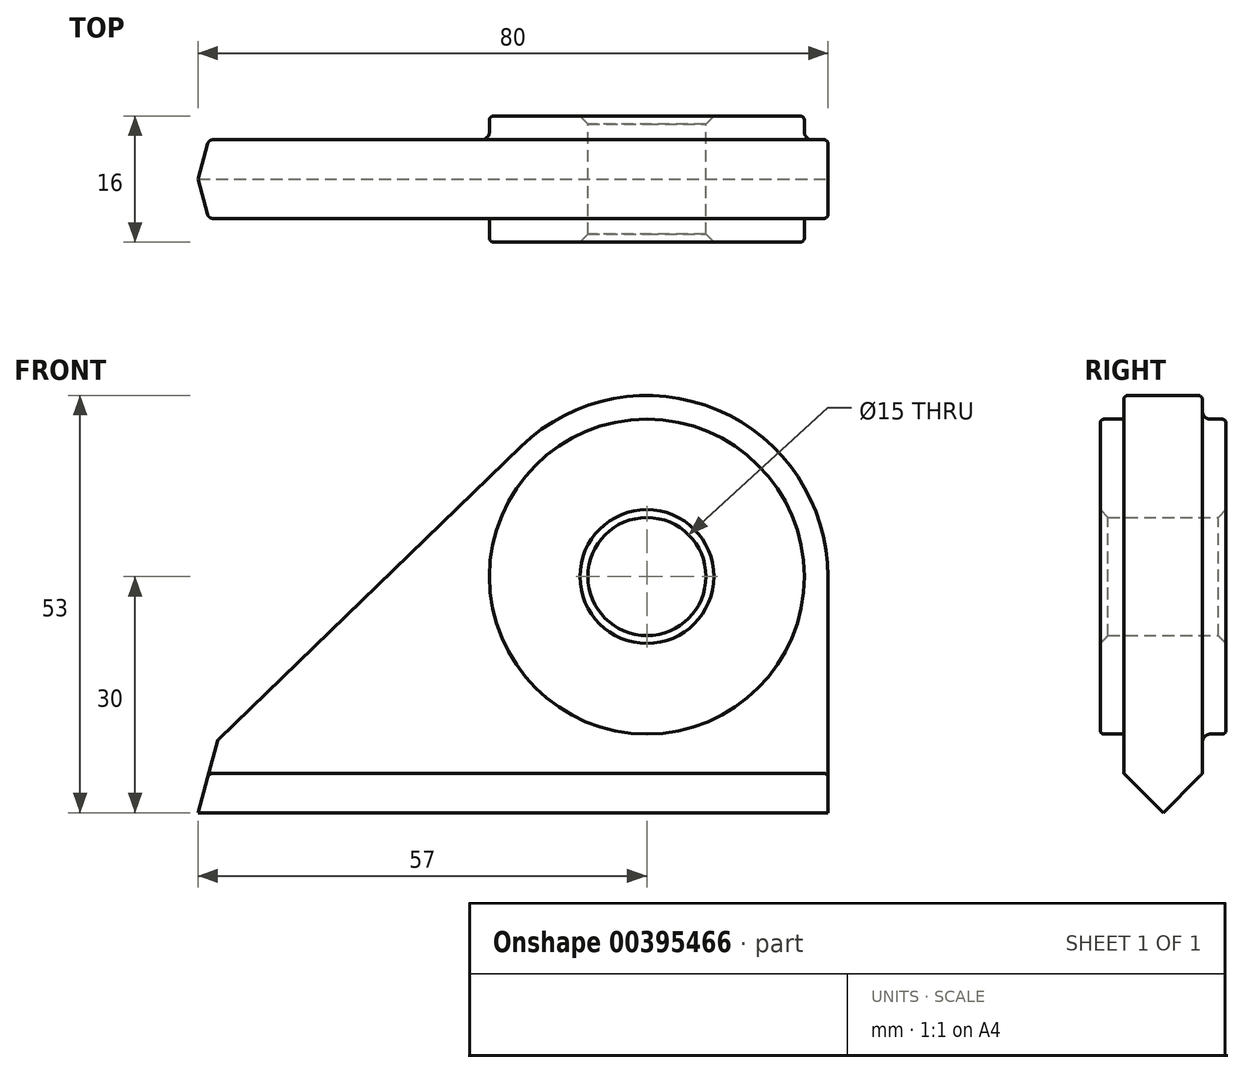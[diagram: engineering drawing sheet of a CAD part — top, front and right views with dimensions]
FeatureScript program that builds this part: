
annotation { "Feature Type Name" : "Feature", "Feature Type Description" : "" }
export const myFeature = defineFeature(function(context is Context, id is Id, definition is map)
    precondition{}
    {
        {
            var Q0;
            Q0=qCreatedBy(makeId("Front.planeOp"),FACE);
            var sketch = newSketch(context, id + "F0", { "sketchPlane" : qUnion([Q0])});
            skCircle(sketch, "E0", {"center": v(0, 0) * mm, "radius": 7.5 * mm});
            skCircle(sketch, "E1", {"center": v(0, 0) * mm, "radius": 20 * mm});
            skArc(sketch, "E2.0", {"start": v(23, 0) * mm, "mid": v(8.98, 21.18) * mm, "end": v(-16, 16.53) * mm});
            skLineSegment(sketch, "E3", {"start": v(23, 0) * mm, "end": v(23, -30) * mm});
            skLineSegment(sketch, "E4", {"start": v(23, -30) * mm, "end": v(-57, -30) * mm});
            skLineSegment(sketch, "E5", {"start": v(-57, -30) * mm, "end": v(-54.52, -20.75) * mm});
            skLineSegment(sketch, "E6", {"start": v(-54.52, -20.75) * mm, "end": v(-16, 16.53) * mm});
            skSolve(sketch);
        }
        {
            var Q0;
            Q0=makeQuery(id+"F0.imprint","IMPRINT",FACE,{"disambiguationData":[TD([[makeQuery(id+"F0.imprint","IMPRINT",EDGE,{"derivedFrom":sQuery(id+"F0.wireOp",EDGE,"E1")}),-1.0]])]});
            extrude(context, id + "F1", {"entities" : qUnion([Q0]), "endBound" : BoundingType.SYMMETRIC, "depth" : 10 * mm});
        }
        {
            var Q0;
            Q0=makeQuery(id+"F0.imprint","IMPRINT",FACE,{"disambiguationData":[TD([[makeQuery(id+"F0.imprint","IMPRINT",EDGE,{"derivedFrom":sQuery(id+"F0.wireOp",EDGE,"E0")}),-1.0]])]});
            extrude(context, id + "F2", {"entities" : qUnion([Q0]), "operationType" : NewBodyOperationType.ADD, "endBound" : BoundingType.SYMMETRIC, "depth" : 16 * mm});
        }
        {
            var Q0;
            Q0=makeQuery(id+"F1.opExtrude","CAP_EDGE",EDGE,{"disambiguationData":[OSD([sQuery(id+"F0.wireOp",EDGE,"E1")])],"isStart":false});
            var Q1;
            Q1=makeQuery(id+"F1.opExtrude","CAP_EDGE",EDGE,{"disambiguationData":[OSD([sQuery(id+"F0.wireOp",EDGE,"E1")])],"isStart":true});
            fillet(context, id + "F3", {"entities" : qUnion([Q0, Q1]), "radius" : 1 * mm, "tangentPropagation" : true, "allowEdgeOverflow" : false});
        }
        {
            var Q0;
            Q0=makeQuery(id+"F2.opExtrude","SWEPT_FACE",FACE,{"disambiguationData":[OSD([sQuery(id+"F0.wireOp",EDGE,"E0")])]});
            chamfer(context, id + "F4", {"entities" : qUnion([Q0]), "width" : 1 * mm, "tangentPropagation" : true});
        }
        {
            var Q0;
            Q0=makeQuery(id+"F1.opExtrude","SWEPT_FACE",FACE,{"disambiguationData":[OSD([sQuery(id+"F0.wireOp",EDGE,"E3")])]});
            var sketch = newSketch(context, id + "F5", { "sketchPlane" : qUnion([Q0])});
            skLineSegment(sketch, "E7", {"start": v(0, 0) * mm, "end": v(0, -30) * mm, "construction": true});
            skLineSegment(sketch, "E8", {"start": v(0, -30) * mm, "end": v(5, -25) * mm});
            skLineSegment(sketch, "E9.MirrorCS", {"start": v(0, -30) * mm, "end": v(-5, -25) * mm});
            skLineSegment(sketch, "E10", {"start": v(5, -25) * mm, "end": v(8.4, -25) * mm});
            skLineSegment(sketch, "E11", {"start": v(8.4, -25) * mm, "end": v(8.4, -34.27) * mm});
            skLineSegment(sketch, "E12", {"start": v(8.4, -34.27) * mm, "end": v(0, -34.27) * mm});
            skLineSegment(sketch, "E13.MirrorCS", {"start": v(-5, -25) * mm, "end": v(-8.4, -25) * mm});
            skLineSegment(sketch, "E14.MirrorCS", {"start": v(-8.4, -25) * mm, "end": v(-8.4, -34.27) * mm});
            skLineSegment(sketch, "E15.MirrorCS", {"start": v(-8.4, -34.27) * mm, "end": v(0, -34.27) * mm});
            skSolve(sketch);
        }
        {
            var Q0;
            Q0 = qSketchRegion(id + "F5", true);
            extrude(context, id + "F6", {"entities" : qUnion([Q0]), "operationType" : NewBodyOperationType.REMOVE, "endBound" : BoundingType.THROUGH_ALL, "oppositeDirection" : true, "depth" : 25 * mm});
        }
        {
            var Q0;
            Q0=makeQuery(id+"F2.opExtrude","CAP_EDGE",EDGE,{"disambiguationData":[OSD([sQuery(id+"F0.wireOp",EDGE,"E1")])],"isStart":false});
            var Q1;
            Q1=makeQuery(id+"F2.opExtrude","CAP_EDGE",EDGE,{"disambiguationData":[OSD([sQuery(id+"F0.wireOp",EDGE,"E1")])],"isStart":true});
            var Q2;
            Q2=makeQuery(id+"F6.boolean.opBoolean","COPY",EDGE,{"derivedFrom":makeQuery(id+"F6.opExtrude","SWEPT_EDGE",EDGE,{"disambiguationData":[OSD([sQuery(id+"F0.wireOp",EDGE,"E3"),sQuery(id+"F5.wireOp",EDGE,"E8"),sQuery(id+"F5.wireOp",EDGE,"E10")])]})});
            var Q3;
            Q3=makeQuery(id+"F1.opExtrude","CAP_EDGE",EDGE,{"disambiguationData":[OSD([sQuery(id+"F0.wireOp",EDGE,"E5")])],"isStart":true});
            var Q4;
            Q4=makeQuery(id+"F1.opExtrude","CAP_EDGE",EDGE,{"disambiguationData":[OSD([sQuery(id+"F0.wireOp",EDGE,"E6")])],"isStart":true});
            var Q5;
            Q5=makeQuery(id+"F6.boolean.opBoolean","COPY",EDGE,{"derivedFrom":makeQuery(id+"F6.opExtrude","SWEPT_EDGE",EDGE,{"disambiguationData":[OSD([sQuery(id+"F0.wireOp",EDGE,"E3"),sQuery(id+"F5.wireOp",EDGE,"E9.MirrorCS"),sQuery(id+"F5.wireOp",EDGE,"E13.MirrorCS")])]})});
            var Q6;
            Q6=makeQuery(id+"F1.opExtrude","CAP_EDGE",EDGE,{"disambiguationData":[OSD([sQuery(id+"F0.wireOp",EDGE,"E5")])],"isStart":false});
            var Q7;
            Q7=makeQuery(id+"F1.opExtrude","CAP_EDGE",EDGE,{"disambiguationData":[OSD([sQuery(id+"F0.wireOp",EDGE,"E3")])],"isStart":false});
            var Q8;
            Q8=makeQuery(id+"F1.opExtrude","SWEPT_EDGE",EDGE,{"disambiguationData":[OSD([sQuery(id+"F0.wireOp",EDGE,"E5"),sQuery(id+"F0.wireOp",EDGE,"E6")])]});
            fillet(context, id + "F7", {"entities" : qUnion([Q0, Q1, Q2, Q3, Q4, Q5, Q6, Q7, Q8]), "radius" : 0.5 * mm, "tangentPropagation" : true, "allowEdgeOverflow" : false});
        }
    });
